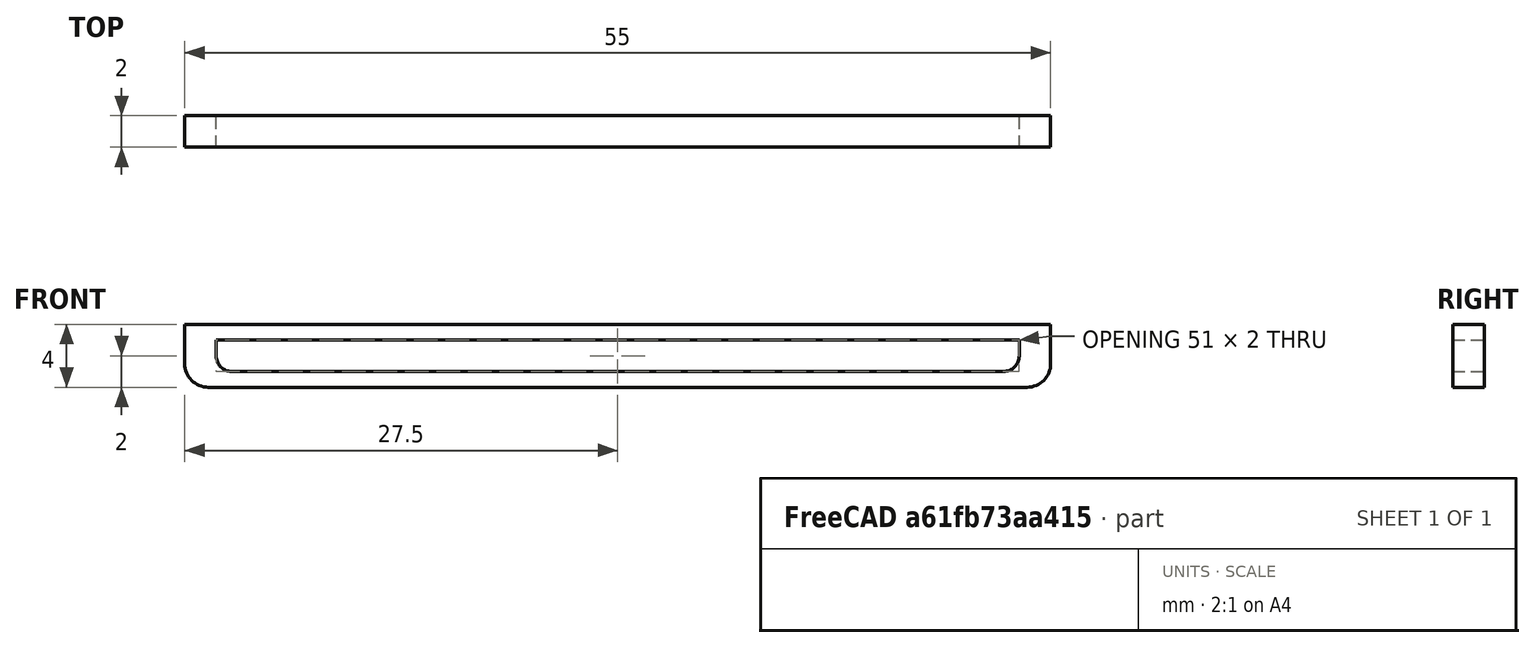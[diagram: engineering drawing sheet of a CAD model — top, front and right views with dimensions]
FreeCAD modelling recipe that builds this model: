
FCSTD DOCUMENT  (FreeCAD 0.18R16146 (Git))
Label: HR_v2_parte_inferior
License: All rights reserved
LicenseURL: http://en.wikipedia.org/wiki/All_rights_reserved
objects: Part::Fillet×3, Part::Box×2, Part::Cut×1
note: 6 computed .brp shape members not serialized (recipe doc carries the construction recipe); baked Part::Feature solids carry a one-line shape summary decoded from their .brp

FEATURE [Part::Box] Box  label="Cube"
  AttacherType = Attacher::AttachEngine3D
  Height = 4
  Length = 55
  Width = 2
FEATURE [Part::Box] Box001  label="Cube001"
  AttacherType = Attacher::AttachEngine3D
  Height = 2
  Length = 51
  Placement = pos=(2,0,1) rot=(0,0,1;0rad)
  Width = 2
FEATURE [Part::Cut] Cut
  Base = -> Box
  Refine = true
  Tool = -> Box001
FEATURE [Part::Fillet] Fillet
  Base = -> Cut
  Edges = 2 edges r=1.5: [Edge4,Edge20]
FEATURE [Part::Fillet] Fillet001
  Base = -> Fillet
  Edges = 1 edges r=1: [Edge30]
FEATURE [Part::Fillet] Fillet002
  Base = -> Fillet001
  Edges = 1 edges r=1: [Edge14]
